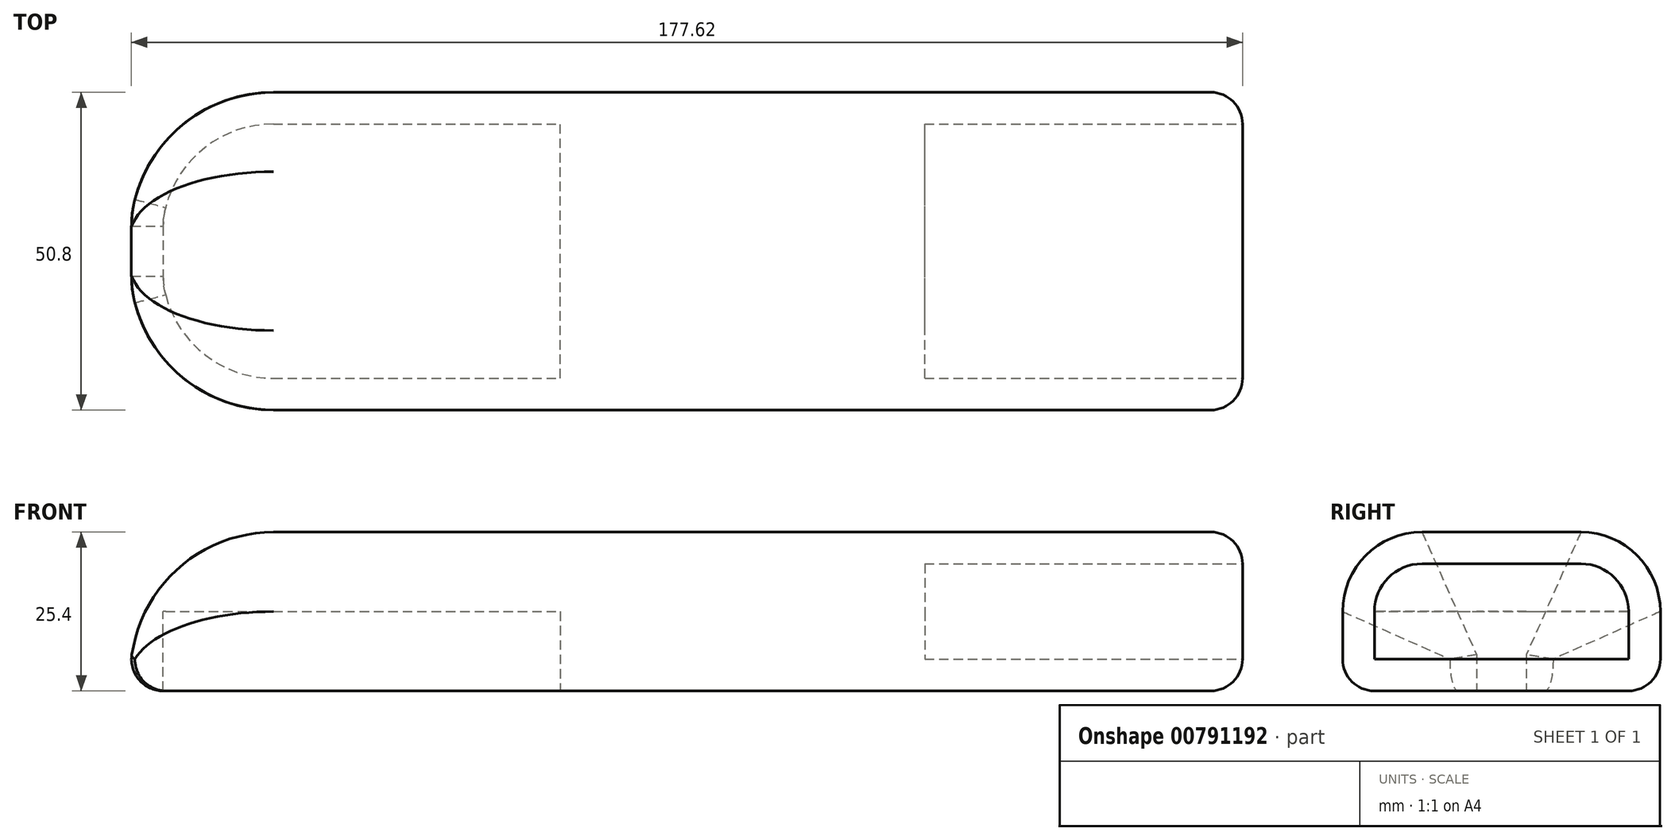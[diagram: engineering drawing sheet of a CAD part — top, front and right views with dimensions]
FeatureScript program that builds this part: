
annotation { "Feature Type Name" : "Feature", "Feature Type Description" : "" }
export const myFeature = defineFeature(function(context is Context, id is Id, definition is map)
    precondition{}
    {
        {
            var Q0;
            Q0=qCreatedBy(makeId("Top.planeOp"),FACE);
            var sketch = newSketch(context, id + "F0", { "sketchPlane" : qUnion([Q0])});
            skLineSegment(sketch, "E0.bottom", {"start": v(-88.9, -25.4) * mm, "end": v(88.9, -25.4) * mm});
            skLineSegment(sketch, "E0.top", {"start": v(-88.9, 25.4) * mm, "end": v(88.9, 25.4) * mm});
            skLineSegment(sketch, "E0.left", {"start": v(-88.9, -25.4) * mm, "end": v(-88.9, 25.4) * mm});
            skLineSegment(sketch, "E0.right", {"start": v(88.9, -25.4) * mm, "end": v(88.9, 25.4) * mm});
            skPoint(sketch, "E0.middle", {"position": v(0, 0) * mm});
            skSolve(sketch);
        }
        {
            var Q0;
            Q0=makeQuery(id+"F0.imprint","IMPRINT",FACE,{"disambiguationData":[TD([[makeQuery(id+"F0.imprint","IMPRINT",EDGE,{"derivedFrom":sQuery(id+"F0.wireOp",EDGE,"E0.bottom")}),1.0]])]});
            extrude(context, id + "F1", {"entities" : qUnion([Q0]), "depth" : 25.4 * mm, "offsetDistance" : 25.4 * mm});
        }
        {
            var Q0;
            Q0=makeQuery(id+"F1.opExtrude","CAP_EDGE",EDGE,{"disambiguationData":[OSD([sQuery(id+"F0.wireOp",EDGE,"E0.top")])],"isStart":false});
            var Q1;
            Q1=makeQuery(id+"F1.opExtrude","CAP_EDGE",EDGE,{"disambiguationData":[OSD([sQuery(id+"F0.wireOp",EDGE,"E0.bottom")])],"isStart":false});
            fillet(context, id + "F2", {"entities" : qUnion([Q0, Q1]), "radius" : 12.7 * mm, "tangentPropagation" : true, "allowEdgeOverflow" : false});
        }
        {
            var Q0;
            Q0=makeQuery(id+"F1.opExtrude","CAP_EDGE",EDGE,{"disambiguationData":[OSD([sQuery(id+"F0.wireOp",EDGE,"E0.left")])],"isStart":false});
            fillet(context, id + "F3", {"entities" : qUnion([Q0]), "radius" : 22.86 * mm, "tangentPropagation" : true, "allowEdgeOverflow" : false});
        }
        {
            var Q0;
            Q0=makeQuery(id+"F1.opExtrude","CAP_EDGE",EDGE,{"disambiguationData":[OSD([sQuery(id+"F0.wireOp",EDGE,"E0.right")])],"isStart":false});
            fillet(context, id + "F4", {"entities" : qUnion([Q0]), "radius" : 5.08 * mm, "tangentPropagation" : true, "allowEdgeOverflow" : false});
        }
        {
            var Q0;
            {var subQ0=sQuery(id+"F0.wireOp",EDGE,"E0.left");var subQ1=sQuery(id+"F0.wireOp",EDGE,"E0.bottom");Q0=makeQuery(id+"F3.opFillet","BLEND_EDGE",EDGE,{"blendedFrom":[makeQuery(id+"F1.opExtrude","SWEPT_EDGE",EDGE,{"disambiguationData":[OSD([subQ1,subQ0])]}),makeQuery(id+"F1.opExtrude","CAP_FACE",FACE,{"disambiguationData":[OSD([subQ1,sQuery(id+"F0.wireOp",EDGE,"E0.top"),subQ0,sQuery(id+"F0.wireOp",EDGE,"E0.right")])],"isStart":true})],"blendedInto":[makeQuery(id+"F1.opExtrude","CAP_FACE",FACE,{"disambiguationData":[OSD([subQ1,sQuery(id+"F0.wireOp",EDGE,"E0.top"),subQ0,sQuery(id+"F0.wireOp",EDGE,"E0.right")])],"isStart":true})]});}
            var Q1;
            {var subQ0=sQuery(id+"F0.wireOp",EDGE,"E0.left");var subQ1=sQuery(id+"F0.wireOp",EDGE,"E0.top");Q1=makeQuery(id+"F3.opFillet","BLEND_EDGE",EDGE,{"blendedFrom":[makeQuery(id+"F1.opExtrude","SWEPT_EDGE",EDGE,{"disambiguationData":[OSD([subQ1,subQ0])]}),makeQuery(id+"F1.opExtrude","CAP_FACE",FACE,{"disambiguationData":[OSD([sQuery(id+"F0.wireOp",EDGE,"E0.bottom"),subQ1,subQ0,sQuery(id+"F0.wireOp",EDGE,"E0.right")])],"isStart":true})],"blendedInto":[makeQuery(id+"F1.opExtrude","CAP_FACE",FACE,{"disambiguationData":[OSD([sQuery(id+"F0.wireOp",EDGE,"E0.bottom"),subQ1,subQ0,sQuery(id+"F0.wireOp",EDGE,"E0.right")])],"isStart":true})]});}
            fillet(context, id + "F5", {"entities" : qUnion([Q0, Q1]), "radius" : 5.08 * mm, "tangentPropagation" : true, "allowEdgeOverflow" : false});
        }
        {
            var Q0;
            Q0=makeQuery(id+"F1.opExtrude","SWEPT_FACE",FACE,{"disambiguationData":[OSD([sQuery(id+"F0.wireOp",EDGE,"E0.right")])]});
            extrude(context, id + "F6", {"entities" : qUnion([Q0]), "operationType" : NewBodyOperationType.REMOVE, "oppositeDirection" : true, "depth" : 50.8 * mm, "offsetDistance" : 25.4 * mm});
        }
        {
            var Q0;
            Q0=makeQuery(id+"F1.opExtrude","CAP_FACE",FACE,{"disambiguationData":[OSD([sQuery(id+"F0.wireOp",EDGE,"E0.bottom"),sQuery(id+"F0.wireOp",EDGE,"E0.top"),sQuery(id+"F0.wireOp",EDGE,"E0.left"),sQuery(id+"F0.wireOp",EDGE,"E0.right")])],"isStart":true});
            var sketch = newSketch(context, id + "F7", { "sketchPlane" : qUnion([Q0])});
            skLineSegment(sketch, "E1", {"start": v(-20.14, 20.32) * mm, "end": v(-20.14, -20.32) * mm});
            skSolve(sketch);
        }
        {
            var Q0;
            {var subQ7=sQuery(id+"F7.wireOp",EDGE,"E1");Q0=makeQuery(id+"F7.imprint","IMPRINT",FACE,{"disambiguationData":[TD([[makeQuery(id+"F7.imprint","IMPRINT",EDGE,{"derivedFrom":subQ7}),-1.0]])]});}
            extrude(context, id + "F8", {"entities" : qUnion([Q0]), "operationType" : NewBodyOperationType.REMOVE, "oppositeDirection" : true, "depth" : 12.7 * mm, "offsetDistance" : 25.4 * mm});
        }
    });
